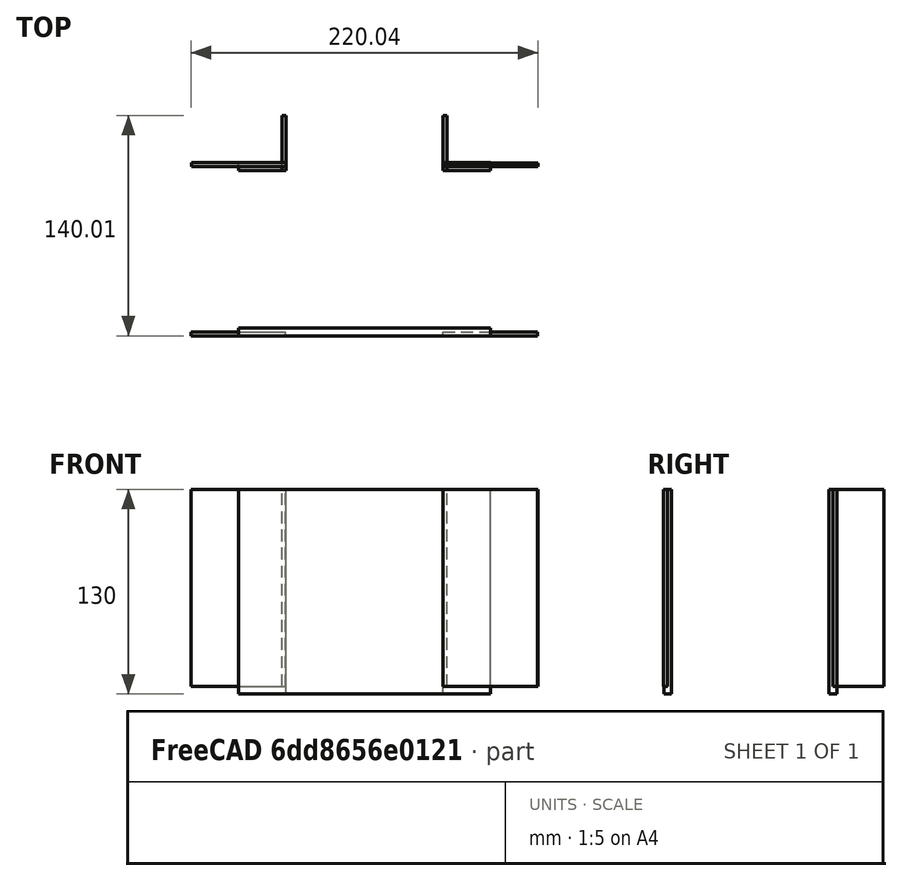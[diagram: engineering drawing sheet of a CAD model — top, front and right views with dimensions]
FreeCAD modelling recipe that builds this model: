
FCSTD DOCUMENT  (FreeCAD 0.19R24291 (Git))
Label: w maze center middle
License: All rights reserved
LicenseURL: http://en.wikipedia.org/wiki/All_rights_reserved
objects: Part::Box×9
note: 9 computed .brp shape members not serialized (recipe doc carries the construction recipe); baked Part::Feature solids carry a one-line shape summary decoded from their .brp

FEATURE [Part::Box] Box004  label="Cube004"
  AttacherType = Attacher::AttachEngine3D
  Height = 130
  Length = 160
  Width = 5
FEATURE [Part::Box] Box015  label="Cube015"
  AttacherType = Attacher::AttachEngine3D
  Height = 130
  Length = 30
  Placement = pos=(0,105,0) rot=(0,0,1;0rad)
  Width = 5
FEATURE [Part::Box] Box016  label="Cube016"
  AttacherType = Attacher::AttachEngine3D
  Height = 130
  Length = 30
  Placement = pos=(130,105,0) rot=(0,0,1;0rad)
  Width = 5
FEATURE [Part::Box] Box007  label="Cube007"
  AttacherType = Attacher::AttachEngine3D
  Height = 125
  Length = 60
  Placement = pos=(130.02,107.426,5.00336) rot=(0,0,1;0rad)
  Width = 2.5
FEATURE [Part::Box] Box006  label="Cube006"
  AttacherType = Attacher::AttachEngine3D
  Height = 125
  Length = 60
  Placement = pos=(129.908,-0.0117223,4.99541) rot=(0,0,1;0rad)
  Width = 2.5
FEATURE [Part::Box] Box018  label="Cube018"
  AttacherType = Attacher::AttachEngine3D
  Height = 125
  Length = 60
  Placement = pos=(-29.8212,107.665,5.00442) rot=(0,0,1;0rad)
  Width = 2.5
FEATURE [Part::Box] Box019  label="Cube019"
  AttacherType = Attacher::AttachEngine3D
  Height = 125
  Length = 60
  Placement = pos=(-30.0202,0.0511968,4.9966) rot=(0,0,1;0rad)
  Width = 2.5
FEATURE [Part::Box] Box010  label="Cube010"
  AttacherType = Attacher::AttachEngine3D
  Height = 125
  Length = 2.5
  Placement = pos=(27.5,105,5) rot=(0,0,1;0rad)
  Width = 35
FEATURE [Part::Box] Box020  label="Cube020"
  AttacherType = Attacher::AttachEngine3D
  Height = 125
  Length = 2.5
  Placement = pos=(130,105,5) rot=(0,0,1;0rad)
  Width = 35
